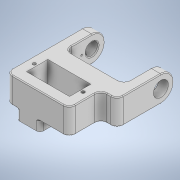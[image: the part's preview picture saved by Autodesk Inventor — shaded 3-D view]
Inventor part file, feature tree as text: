
AUTODESK INVENTOR PART (.ipt)
format: ipt  version: 2020.3 (Build 243373000, 373)  size: 354,816 bytes
history: native  units: mm
features: sketch x5, other x3
ambient origin geometry x8: Origin, YZ Plane, XZ Plane, XY Plane, X Axis, Y Axis, Z Axis, Center Point
bodies: Solid1 (feature_tree)
feature tree (8):
  other  "LegStart_v1.ipt"
  other  "Solid1::LegStart_v1.ipt"
  other  "TaggingFeature1"
  sketch  "Sketch1"  dims[d0=10.0mm]
  sketch  "Sketch2"
  sketch  "Sketch3"
  sketch  "Sketch8"
  sketch  "Sketch9"
